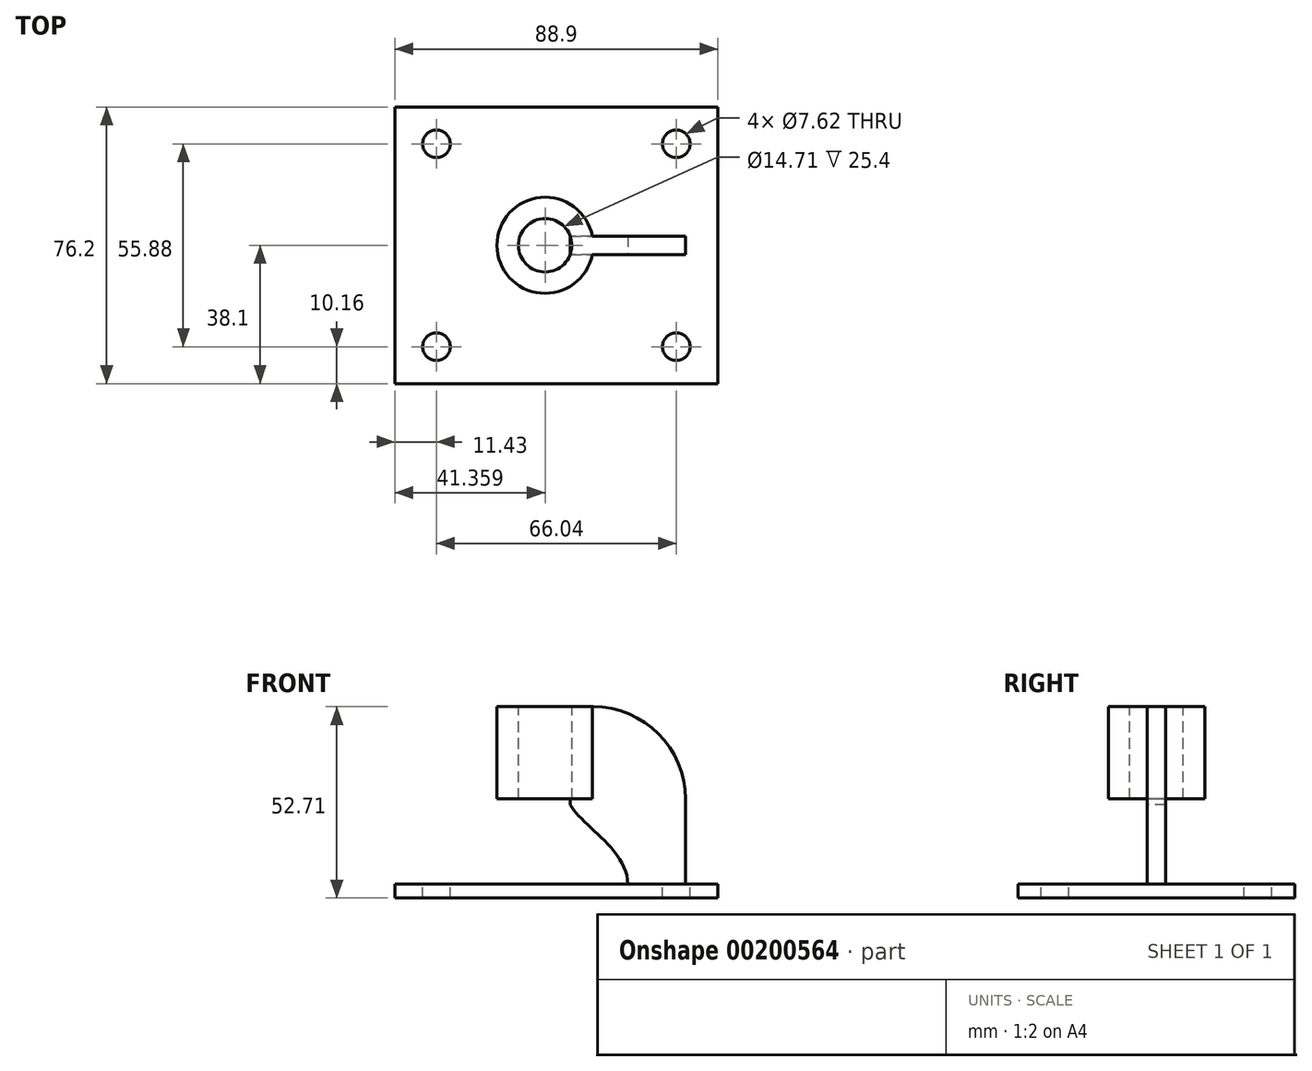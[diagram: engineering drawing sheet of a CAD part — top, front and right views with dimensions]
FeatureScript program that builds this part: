
annotation { "Feature Type Name" : "Feature", "Feature Type Description" : "" }
export const myFeature = defineFeature(function(context is Context, id is Id, definition is map)
    precondition{}
    {
        {
            var Q0;
            Q0=qCreatedBy(makeId("Top.planeOp"),FACE);
            var sketch = newSketch(context, id + "F0", { "sketchPlane" : qUnion([Q0])});
            skLineSegment(sketch, "E0.bottom", {"start": v(0, 0) * mm, "end": v(88.9, 0) * mm});
            skLineSegment(sketch, "E0.top", {"start": v(0, -76.2) * mm, "end": v(88.9, -76.2) * mm});
            skLineSegment(sketch, "E0.left", {"start": v(0, 0) * mm, "end": v(0, -76.2) * mm});
            skLineSegment(sketch, "E0.right", {"start": v(88.9, 0) * mm, "end": v(88.9, -76.2) * mm});
            skSolve(sketch);
        }
        {
            var Q0;
            Q0 = qSketchRegion(id + "F0", true);
            extrude(context, id + "F1", {"entities" : qUnion([Q0]), "depth" : 3.8 * mm});
        }
        {
            var Q0;
            Q0=makeQuery(id+"F1.opExtrude","SWEPT_FACE",FACE,{"disambiguationData":[OSD([sQuery(id+"F0.wireOp",EDGE,"E0.top")])]});
            var Q1;
            Q1=makeQuery(id+"F1.opExtrude","SWEPT_FACE",FACE,{"disambiguationData":[OSD([sQuery(id+"F0.wireOp",EDGE,"E0.bottom")])]});
            cPlane(context, id + "F2", {"entities" : qUnion([Q0, Q1]), "cplaneType" : CPlaneType.MID_PLANE, "offset" : 25.4 * mm, "width" : 152.4 * mm, "height" : 152.4 * mm});
        }
        {
            var Q0;
            Q0=qCreatedBy(id+"F2.planeOp",FACE);
            var sketch = newSketch(context, id + "F3", { "sketchPlane" : qUnion([Q0])});
            skLineSegment(sketch, "E1.bottom", {"start": v(80.01, 1.9) * mm, "end": v(48.26, 1.9) * mm});
            skLineSegment(sketch, "E1.top", {"start": v(54.61, 52.7) * mm, "end": v(48.26, 52.7) * mm});
            skLineSegment(sketch, "E1.left", {"start": v(80.01, 1.9) * mm, "end": v(80.01, 27.3) * mm});
            skLineSegment(sketch, "E1.right", {"start": v(48.26, 1.9) * mm, "end": v(48.26, 52.7) * mm});
            skPoint(sketch, "E2.visualSharp", {"position": v(80, 52.7) * mm});
            skArc(sketch, "E2.filletArc", {"start": v(80.01, 27.3) * mm, "mid": v(72.57, 45.27) * mm, "end": v(54.61, 52.7) * mm});
            skSolve(sketch);
        }
        {
            var Q0;
            Q0 = qSketchRegion(id + "F3", true);
            extrude(context, id + "F4", {"entities" : qUnion([Q0]), "operationType" : NewBodyOperationType.ADD, "depth" : 2.54 * mm, "hasSecondDirection" : true, "secondDirectionOppositeDirection" : true, "secondDirectionDepth" : 2.54 * mm});
        }
        {
            var Q0;
            Q0=makeQuery(id+"F4.opExtrude","CAP_FACE",FACE,{"disambiguationData":[OSD([sQuery(id+"F3.wireOp",EDGE,"E1.bottom"),sQuery(id+"F3.wireOp",EDGE,"E1.top"),sQuery(id+"F3.wireOp",EDGE,"E1.left"),sQuery(id+"F3.wireOp",EDGE,"E1.right"),sQuery(id+"F3.wireOp",EDGE,"E2.filletArc")])],"isStart":false});
            var sketch = newSketch(context, id + "F5", { "sketchPlane" : qUnion([Q0])});
            skFitSpline(sketch, "E3", {"points": [v(48.26, 35.74) * mm, v(47.63, 28) * mm, v(64.13, 3.81) * mm], "startDerivative": vector(32.42, -12.48) * mm, "endDerivative": vector(0.74, -49.74) * mm});
            skLineSegment(sketch, "E4", {"start": v(48.26, 35.74) * mm, "end": v(48.26, 3.81) * mm});
            skLineSegment(sketch, "E5", {"start": v(48.26, 3.81) * mm, "end": v(64.13, 3.81) * mm});
            skSolve(sketch);
        }
        {
            var Q0;
            Q0 = qSketchRegion(id + "F5", true);
            var Q1;
            Q1=makeQuery(id+"F4.opExtrude","CAP_FACE",FACE,{"disambiguationData":[OSD([sQuery(id+"F3.wireOp",EDGE,"E1.bottom"),sQuery(id+"F3.wireOp",EDGE,"E1.top"),sQuery(id+"F3.wireOp",EDGE,"E1.left"),sQuery(id+"F3.wireOp",EDGE,"E1.right"),sQuery(id+"F3.wireOp",EDGE,"E2.filletArc")])],"isStart":true});
            extrude(context, id + "F6", {"entities" : qUnion([Q0]), "operationType" : NewBodyOperationType.REMOVE, "endBound" : BoundingType.UP_TO_SURFACE, "oppositeDirection" : true, "endBoundEntityFace" : qUnion([Q1]), "depth" : 25.4 * mm});
        }
        {
            var Q0;
            Q0=makeQuery(id+"F4.opExtrude","SWEPT_FACE",FACE,{"disambiguationData":[OSD([sQuery(id+"F3.wireOp",EDGE,"E1.top")])]});
            var sketch = newSketch(context, id + "F7", { "sketchPlane" : qUnion([Q0])});
            skCircle(sketch, "E6", {"center": v(41.36, -38.1) * mm, "radius": 7.35 * mm});
            skPoint(sketch, "E6.centerSnap0", {"position": v(48.26, -38.1) * mm});
            skSolve(sketch);
        }
        {
            var Q0;
            Q0 = qSketchRegion(id + "F7", true);
            extrude(context, id + "F8", {"entities" : qUnion([Q0]), "operationType" : NewBodyOperationType.REMOVE, "oppositeDirection" : true, "depth" : 25.4 * mm});
        }
        {
            var Q0;
            Q0=makeQuery(id+"F4.opExtrude","SWEPT_FACE",FACE,{"disambiguationData":[OSD([sQuery(id+"F3.wireOp",EDGE,"E1.top")])]});
            var sketch = newSketch(context, id + "F9", { "sketchPlane" : qUnion([Q0])});
            skCircle(sketch, "E7", {"center": v(41.36, -38.1) * mm, "radius": 7.35 * mm});
            skCircle(sketch, "E8", {"center": v(41.36, -38.1) * mm, "radius": 13.25 * mm});
            skSolve(sketch);
        }
        {
            var Q0;
            Q0 = qSketchRegion(id + "F9", true);
            extrude(context, id + "F10", {"entities" : qUnion([Q0]), "operationType" : NewBodyOperationType.ADD, "oppositeDirection" : true, "depth" : 25.4 * mm});
        }
        {
            var Q0;
            Q0=makeQuery(id+"F6.boolean.opBoolean","MERGE",FACE,{"derivedFrom":[makeQuery(id+"F1.opExtrude","CAP_FACE",FACE,{"disambiguationData":[OSD([sQuery(id+"F0.wireOp",EDGE,"E0.bottom"),sQuery(id+"F0.wireOp",EDGE,"E0.top"),sQuery(id+"F0.wireOp",EDGE,"E0.left"),sQuery(id+"F0.wireOp",EDGE,"E0.right")])],"isStart":false}),makeQuery(id+"F6.opExtrude","SWEPT_FACE",FACE,{"disambiguationData":[OSD([sQuery(id+"F5.wireOp",EDGE,"E5")])]})]});
            var sketch = newSketch(context, id + "F11", { "sketchPlane" : qUnion([Q0])});
            skCircle(sketch, "E9", {"center": v(11.43, -10.16) * mm, "radius": 3.81 * mm});
            skCircle(sketch, "E10", {"center": v(77.47, -10.16) * mm, "radius": 3.81 * mm});
            skCircle(sketch, "E11", {"center": v(77.47, -66.04) * mm, "radius": 3.81 * mm});
            skCircle(sketch, "E12", {"center": v(11.43, -66.04) * mm, "radius": 3.81 * mm});
            skSolve(sketch);
        }
        {
            var Q0;
            Q0 = qSketchRegion(id + "F11", true);
            extrude(context, id + "F12", {"entities" : qUnion([Q0]), "operationType" : NewBodyOperationType.REMOVE, "oppositeDirection" : true, "depth" : 25.4 * mm});
        }
    });
